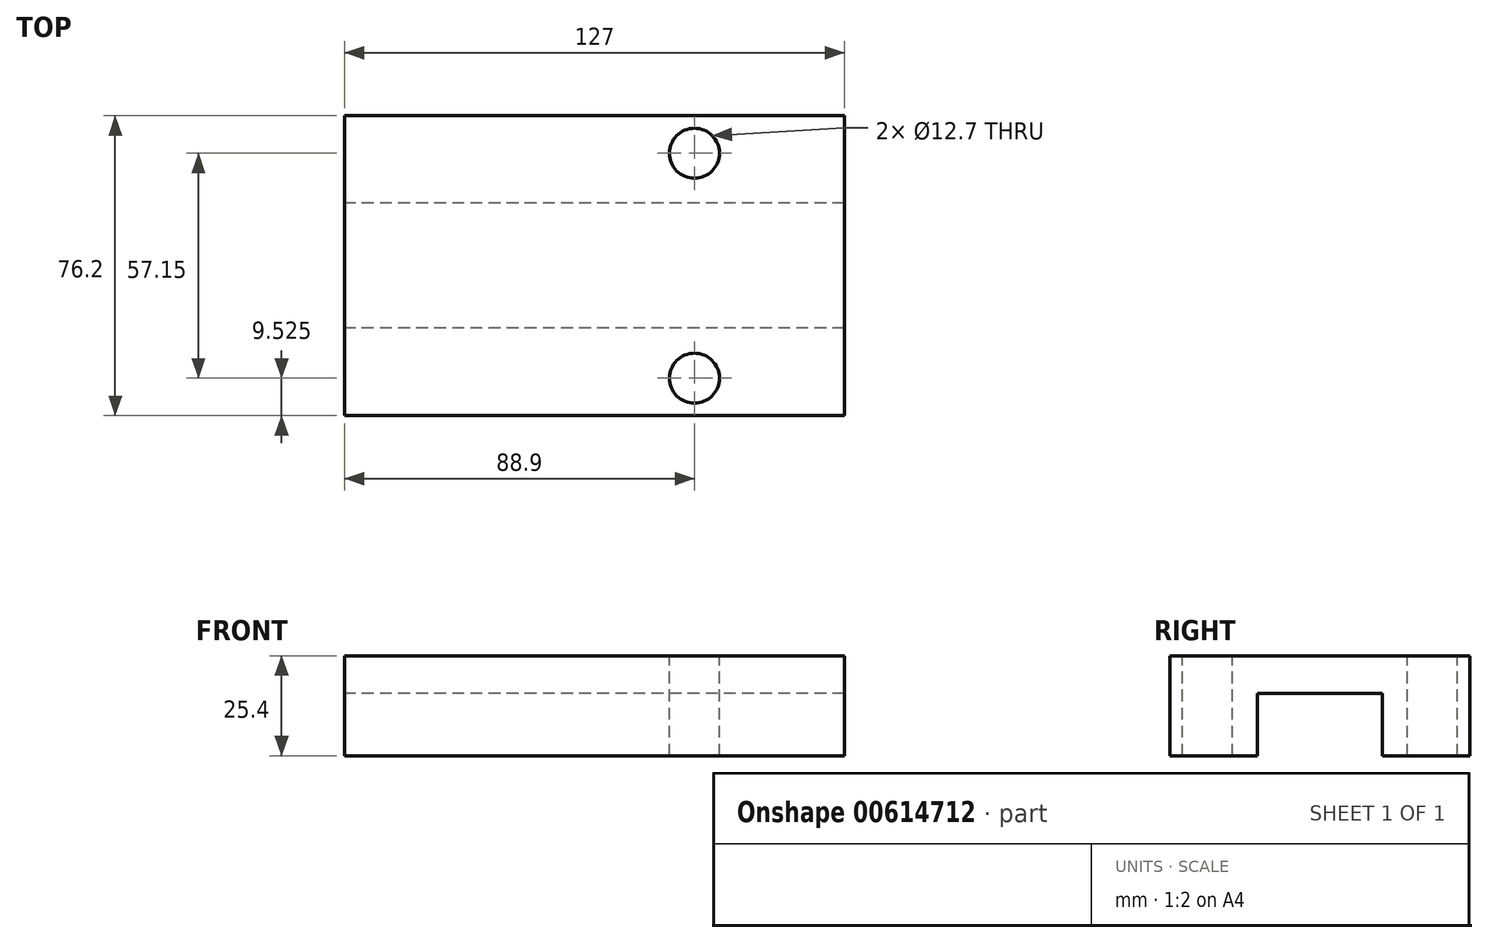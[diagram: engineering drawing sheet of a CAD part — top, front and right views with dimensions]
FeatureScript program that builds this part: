
annotation { "Feature Type Name" : "Feature", "Feature Type Description" : "" }
export const myFeature = defineFeature(function(context is Context, id is Id, definition is map)
    precondition{}
    {
        {
            var Q0;
            Q0=qCreatedBy(makeId("Top.planeOp"),FACE);
            var sketch = newSketch(context, id + "F0", { "sketchPlane" : qUnion([Q0])});
            skLineSegment(sketch, "E0.bottom", {"start": v(63.5, -38.1) * mm, "end": v(-63.5, -38.1) * mm});
            skLineSegment(sketch, "E0.top", {"start": v(63.5, 38.1) * mm, "end": v(-63.5, 38.1) * mm});
            skLineSegment(sketch, "E0.left", {"start": v(63.5, -38.1) * mm, "end": v(63.5, 38.1) * mm});
            skLineSegment(sketch, "E0.right", {"start": v(-63.5, -38.1) * mm, "end": v(-63.5, 38.1) * mm});
            skPoint(sketch, "E0.middle", {"position": v(0, 0) * mm});
            skSolve(sketch);
        }
        {
            var Q0;
            Q0 = qSketchRegion(id + "F0", true);
            extrude(context, id + "F1", {"entities" : qUnion([Q0]), "depth" : 25.4 * mm, "offsetDistance" : 25.4 * mm});
        }
        {
            var Q0;
            Q0=makeQuery(id+"F1.opExtrude","CAP_FACE",FACE,{"disambiguationData":[OSD([sQuery(id+"F0.wireOp",EDGE,"E0.bottom"),sQuery(id+"F0.wireOp",EDGE,"E0.top"),sQuery(id+"F0.wireOp",EDGE,"E0.left"),sQuery(id+"F0.wireOp",EDGE,"E0.right")])],"isStart":true});
            var sketch = newSketch(context, id + "F2", { "sketchPlane" : qUnion([Q0])});
            skLineSegment(sketch, "E1.bottom", {"start": v(63.5, -15.87) * mm, "end": v(-63.5, -15.87) * mm});
            skLineSegment(sketch, "E1.top", {"start": v(63.5, 15.88) * mm, "end": v(-63.5, 15.88) * mm});
            skLineSegment(sketch, "E1.left", {"start": v(63.5, -15.87) * mm, "end": v(63.5, 15.88) * mm});
            skLineSegment(sketch, "E1.right", {"start": v(-63.5, -15.87) * mm, "end": v(-63.5, 15.88) * mm});
            skPoint(sketch, "E1.middle", {"position": v(0, 0) * mm});
            skSolve(sketch);
        }
        {
            var Q0;
            Q0 = qSketchRegion(id + "F2", true);
            extrude(context, id + "F3", {"entities" : qUnion([Q0]), "operationType" : NewBodyOperationType.REMOVE, "oppositeDirection" : true, "depth" : 15.88 * mm, "offsetDistance" : 25.4 * mm});
        }
        {
            var Q0;
            Q0=makeQuery(id+"F1.opExtrude","CAP_FACE",FACE,{"disambiguationData":[OSD([sQuery(id+"F0.wireOp",EDGE,"E0.bottom"),sQuery(id+"F0.wireOp",EDGE,"E0.top"),sQuery(id+"F0.wireOp",EDGE,"E0.left"),sQuery(id+"F0.wireOp",EDGE,"E0.right")])],"isStart":false});
            var sketch = newSketch(context, id + "F4", { "sketchPlane" : qUnion([Q0])});
            skCircle(sketch, "E2", {"center": v(25.4, 28.57) * mm, "radius": 6.35 * mm});
            skCircle(sketch, "E3", {"center": v(25.4, -28.58) * mm, "radius": 6.35 * mm});
            skSolve(sketch);
        }
        {
            var Q0;
            Q0 = qSketchRegion(id + "F4", true);
            extrude(context, id + "F5", {"entities" : qUnion([Q0]), "operationType" : NewBodyOperationType.REMOVE, "endBound" : BoundingType.THROUGH_ALL, "oppositeDirection" : true, "depth" : 25.4 * mm, "offsetDistance" : 25.4 * mm});
        }
    });
